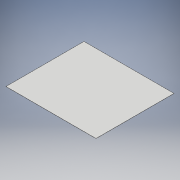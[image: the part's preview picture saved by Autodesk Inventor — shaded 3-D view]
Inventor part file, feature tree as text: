
AUTODESK INVENTOR PART (.ipt)
format: ipt  version: 2017 (Build 210142000, 142)  size: 93,696 bytes
history: native  units: mm
features: sheet_metal_op x1, sketch x1, other x1
ambient origin geometry x8: Origin, YZ Plane, XZ Plane, XY Plane, X Axis, Y Axis, Z Axis, Center Point
bodies: Solid1 (feature_tree)
feature tree (3):
  sheet_metal_op  "Face1"
  sketch  "Sketch1"  dims[d0=300.0mm d1=260.0mm d2=0.5mm]
  other  "Plate1"
